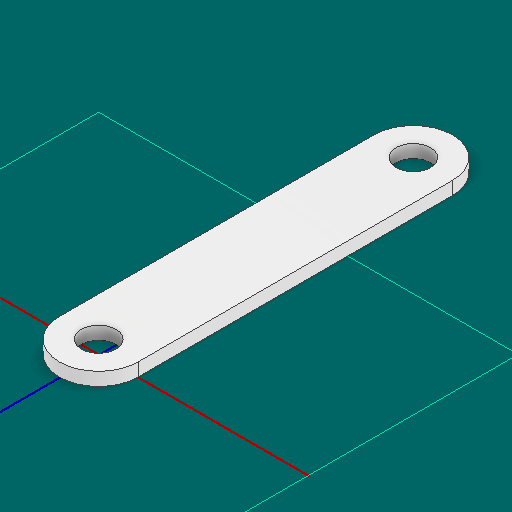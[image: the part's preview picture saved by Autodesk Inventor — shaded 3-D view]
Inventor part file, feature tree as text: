
AUTODESK INVENTOR PART (.ipt)
format: ipt  version: 2025 (Build 290162000, 162)  size: 104,448 bytes
history: native  units: in
note: dims shown in document units (in); Inventor stores cm internally (conversion verified against a paired STEP export)
features: extrude x1, sketch x1
ambient origin geometry x8: Origin, YZ Plane, XZ Plane, XY Plane, X Axis, Y Axis, Z Axis, Center Point
bodies: Solid1 (feature_tree)
feature tree (2):
  extrude  "Extrusion1"  Depth=1.5in
  sketch  "Sketch2"  dims[d0=0.165in d1=0.105in d2=0.165in d3=0.0625in d4=0.0in d5=1.5in]
